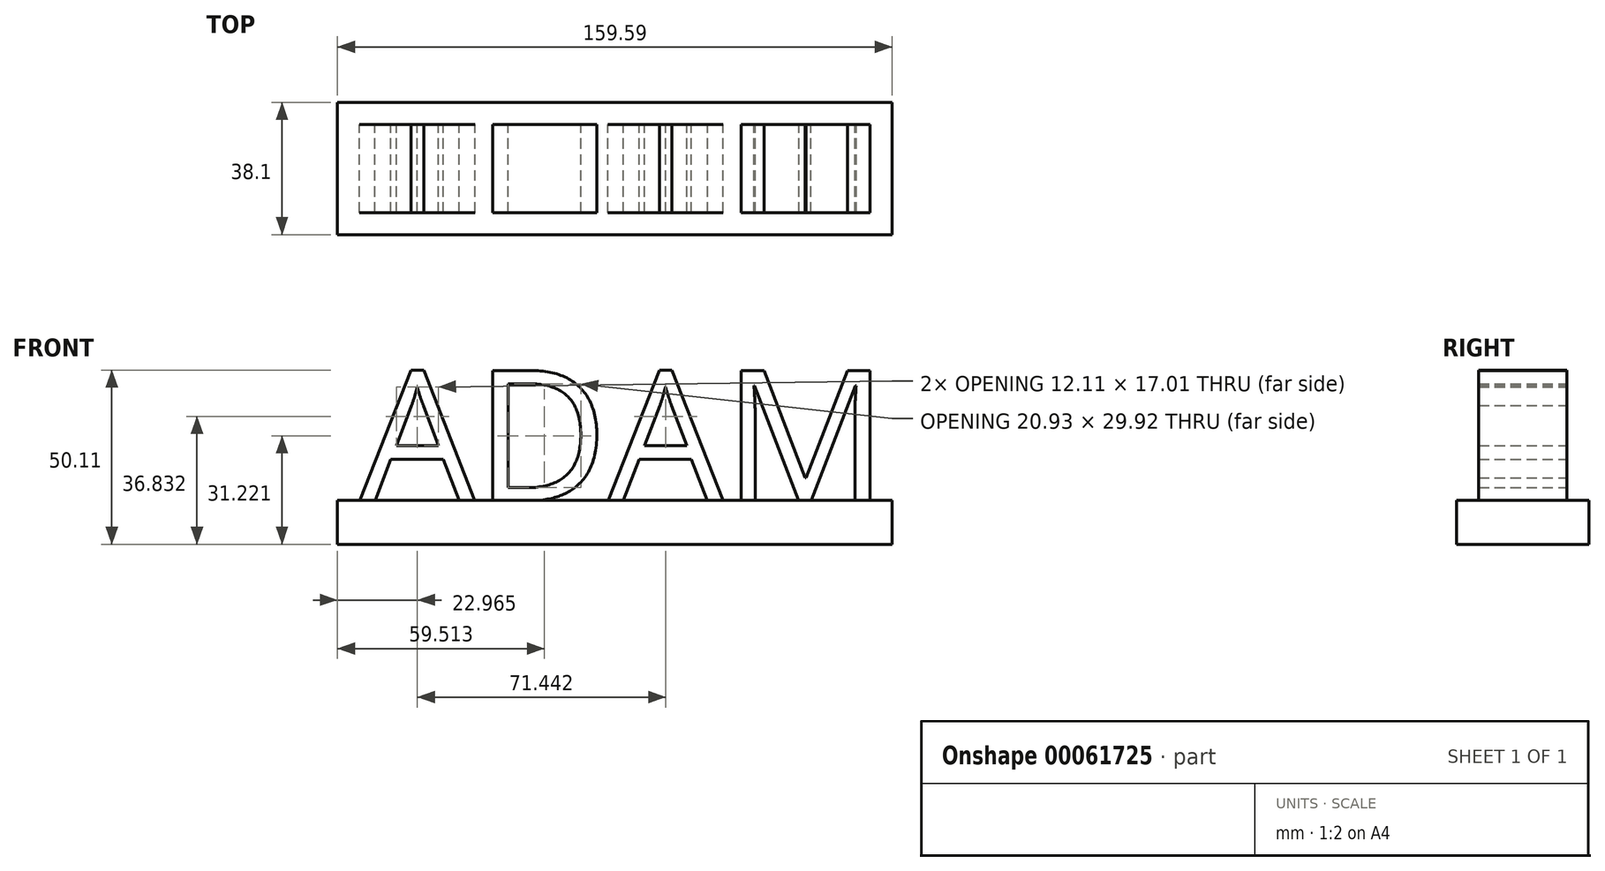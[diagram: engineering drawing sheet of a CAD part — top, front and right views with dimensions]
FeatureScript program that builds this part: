
annotation { "Feature Type Name" : "Feature", "Feature Type Description" : "" }
export const myFeature = defineFeature(function(context is Context, id is Id, definition is map)
    precondition{}
    {
        {
            var Q0;
            Q0=qCreatedBy(makeId("Front.planeOp"),FACE);
            var sketch = newSketch(context, id + "F0", { "sketchPlane" : qUnion([Q0])});
            skText(sketch, "E0", { "text": "ADAM", "fontName": "OpenSans-Regular.ttf"});
            const initialGuessF0  = {"E0": [0, -0.0002, 1, 0, 0.03777]};
            skSetInitialGuess(sketch, initialGuessF0);
            skSolve(sketch);
        }
        {
            var Q0;
            Q0 = qSketchRegion(id + "F0", true);
            extrude(context, id + "F1", {"entities" : qUnion([Q0]), "depth" : 25.4 * mm});
        }
        {
            var Q0;
            Q0=qCreatedBy(makeId("Front.planeOp"),FACE);
            var sketch = newSketch(context, id + "F2", { "sketchPlane" : qUnion([Q0])});
            skLineSegment(sketch, "E1.bottom", {"start": v(-6.35, 0) * mm, "end": v(153.24, 0) * mm});
            skLineSegment(sketch, "E1.top", {"start": v(-6.35, -12.7) * mm, "end": v(153.24, -12.7) * mm});
            skLineSegment(sketch, "E1.left", {"start": v(-6.35, 0) * mm, "end": v(-6.35, -12.7) * mm});
            skLineSegment(sketch, "E1.right", {"start": v(153.24, 0) * mm, "end": v(153.24, -12.7) * mm});
            skSolve(sketch);
        }
        {
            var Q0;
            Q0 = qSketchRegion(id + "F2", true);
            extrude(context, id + "F3", {"entities" : qUnion([Q0]), "depth" : 31.75 * mm, "hasSecondDirection" : true, "secondDirectionOppositeDirection" : true, "secondDirectionDepth" : 6.35 * mm});
        }
    });
